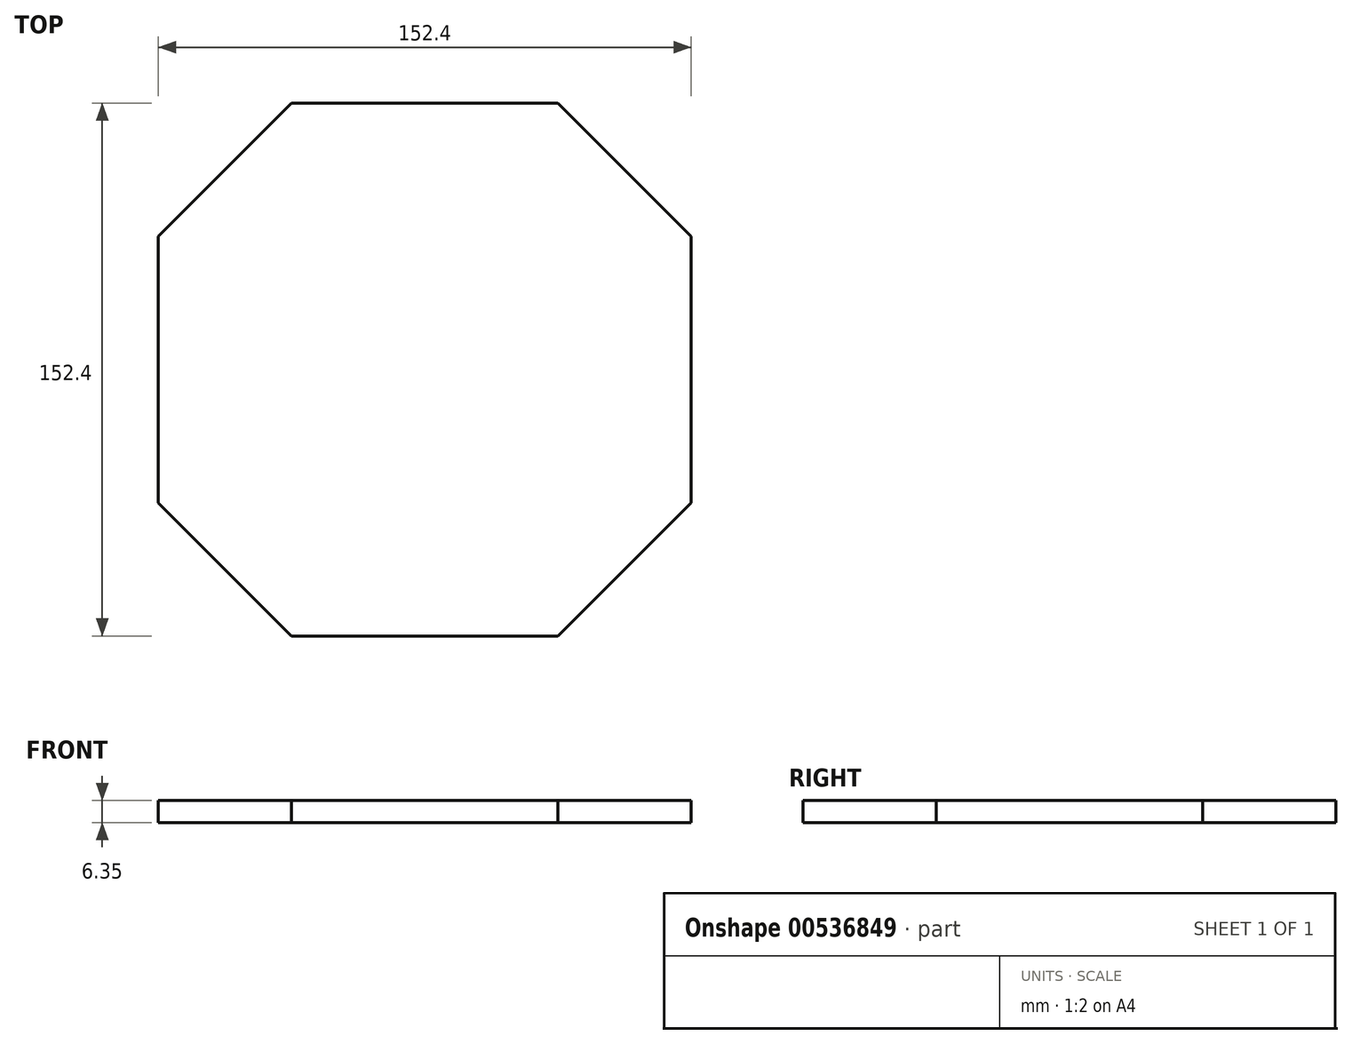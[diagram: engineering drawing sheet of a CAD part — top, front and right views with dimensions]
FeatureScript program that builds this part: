
annotation { "Feature Type Name" : "Feature", "Feature Type Description" : "" }
export const myFeature = defineFeature(function(context is Context, id is Id, definition is map)
    precondition{}
    {
        {
            var Q0;
            Q0=qCreatedBy(makeId("Top.planeOp"),FACE);
            var sketch = newSketch(context, id + "F0", { "sketchPlane" : qUnion([Q0])});
            skLineSegment(sketch, "E0", {"start": v(0, 0) * mm, "end": v(-76.2, 0) * mm});
            skLineSegment(sketch, "E1", {"start": v(0, 0) * mm, "end": v(76.2, 0) * mm});
            skLineSegment(sketch, "E2", {"start": v(0, 0) * mm, "end": v(0, 76.2) * mm});
            skLineSegment(sketch, "E3", {"start": v(0, 0) * mm, "end": v(0, -76.2) * mm});
            skLineSegment(sketch, "E4", {"start": v(-76.2, 0) * mm, "end": v(-76.2, 38.1) * mm});
            skLineSegment(sketch, "E5", {"start": v(-76.2, 0) * mm, "end": v(-76.2, -38.1) * mm});
            skLineSegment(sketch, "E6", {"start": v(0, 76.2) * mm, "end": v(-38.1, 76.2) * mm});
            skLineSegment(sketch, "E7", {"start": v(-38.1, 76.2) * mm, "end": v(-76.2, 38.1) * mm});
            skLineSegment(sketch, "E8", {"start": v(0, 76.2) * mm, "end": v(38.1, 76.2) * mm});
            skLineSegment(sketch, "E9", {"start": v(76.2, 0) * mm, "end": v(76.2, 38.1) * mm});
            skLineSegment(sketch, "E10", {"start": v(38.1, 76.2) * mm, "end": v(76.2, 38.1) * mm});
            skLineSegment(sketch, "E11", {"start": v(0, -76.2) * mm, "end": v(-38.1, -76.2) * mm});
            skLineSegment(sketch, "E12", {"start": v(-76.2, -38.1) * mm, "end": v(-38.1, -76.2) * mm});
            skLineSegment(sketch, "E13", {"start": v(76.2, 0) * mm, "end": v(76.2, -38.1) * mm});
            skLineSegment(sketch, "E14", {"start": v(0, -76.2) * mm, "end": v(38.1, -76.2) * mm});
            skLineSegment(sketch, "E15", {"start": v(38.1, -76.2) * mm, "end": v(76.2, -38.1) * mm});
            skSolve(sketch);
        }
        {
            var Q0;
            Q0 = qSketchRegion(id + "F0", true);
            extrude(context, id + "F1", {"entities" : qUnion([Q0]), "depth" : 6.35 * mm, "offsetDistance" : 25.4 * mm});
        }
    });
